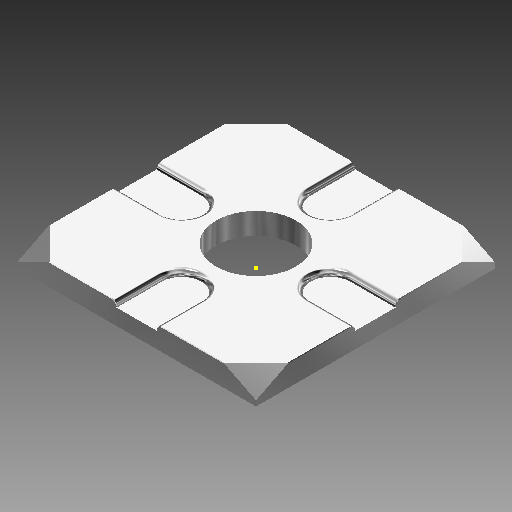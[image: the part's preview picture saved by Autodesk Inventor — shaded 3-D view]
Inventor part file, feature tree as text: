
AUTODESK INVENTOR PART (.ipt)
format: ipt  version: 2019 (Build 230136000, 136)  size: 226,304 bytes
history: native  units: in
note: dims shown in document units (in); Inventor stores cm internally (conversion verified against a paired STEP export)
features: sketch x4, extrude x3, fillet x2, chamfer x2
ambient origin geometry x8: Origin, YZ Plane, XZ Plane, XY Plane, X Axis, Y Axis, Z Axis, Center Point
bodies: Solid1 (feature_tree)
feature tree (11):
  extrude  "Extrusion1"  Depth=0.042in TaperAngle=0.0deg
  extrude  "Extrusion2"  Depth=0.077in
  fillet  "Fillet1"  Radius=0.0385in
  sketch  "Sketch3"  dims[d6=0.077in d7=0.126in]
  extrude  "Extrusion3"  Depth=0.126in
  chamfer  "Chamfer1"  Distance=0.126in
  chamfer  "Chamfer2"  Distance=0.0385in
  fillet  "Fillet2"  Radius=0.126in
  sketch  "Sketch1"  dims[d0=0.464in d1=0.042in d2=0.0in]
  sketch  "Sketch2"  dims[d3=0.126in d4=0.077in d5=0.0385in]
  sketch  "Sketch4"  dims[d8=0.0385in d9=0.126in d10=0.0385in d11=0.126in d12=0.0385in d13=0.011in d14=0.0in d15=0.011in d16=0.155in d17=0.011in d18=0.0in d19=0.001in d20=0.125in d21=45.0deg d22=0.05in d23=0.125in d24=45.0deg d25=0.001in]
